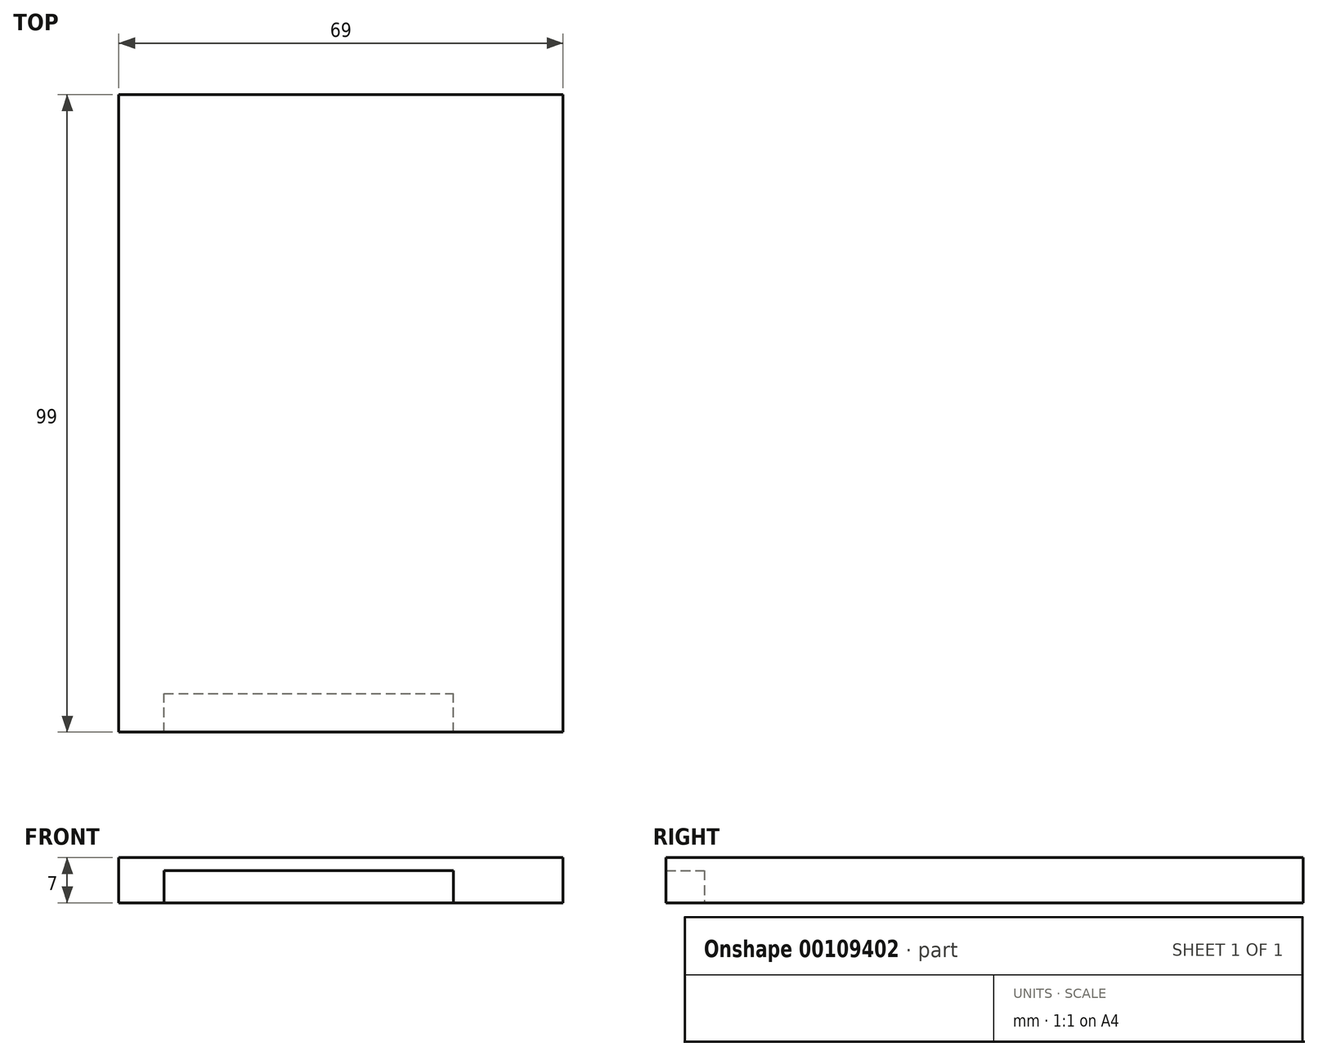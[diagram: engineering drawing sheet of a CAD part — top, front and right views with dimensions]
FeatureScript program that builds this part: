
annotation { "Feature Type Name" : "Feature", "Feature Type Description" : "" }
export const myFeature = defineFeature(function(context is Context, id is Id, definition is map)
    precondition{}
    {
        {
            var Q0;
            Q0=qCreatedBy(makeId("Top.planeOp"),FACE);
            var sketch = newSketch(context, id + "F0", { "sketchPlane" : qUnion([Q0])});
            skLineSegment(sketch, "E0.bottom", {"start": v(34.5, -49.5) * mm, "end": v(-34.5, -49.5) * mm});
            skLineSegment(sketch, "E0.top", {"start": v(34.5, 49.5) * mm, "end": v(-34.5, 49.5) * mm});
            skLineSegment(sketch, "E0.left", {"start": v(34.5, -49.5) * mm, "end": v(34.5, 49.5) * mm});
            skLineSegment(sketch, "E0.right", {"start": v(-34.5, -49.5) * mm, "end": v(-34.5, 49.5) * mm});
            skPoint(sketch, "E0.middle", {"position": v(0, 0) * mm});
            skSolve(sketch);
        }
        {
            var Q0;
            Q0 = qSketchRegion(id + "F0", true);
            extrude(context, id + "F2", {"entities" : qUnion([Q0]), "endBound" : BoundingType.SYMMETRIC, "depth" : 7 * mm});
        }
        {
            var Q0;
            Q0=makeQuery(id+"F2.opExtrude","CAP_FACE",FACE,{"disambiguationData":[OSD([sQuery(id+"F0.wireOp",EDGE,"E0.bottom"),sQuery(id+"F0.wireOp",EDGE,"E0.top"),sQuery(id+"F0.wireOp",EDGE,"E0.left"),sQuery(id+"F0.wireOp",EDGE,"E0.right")])],"isStart":true});
            var sketch = newSketch(context, id + "F1", { "sketchPlane" : qUnion([Q0])});
            skLineSegment(sketch, "E1.bottom", {"start": v(-27.5, 49.5) * mm, "end": v(17.5, 49.5) * mm});
            skLineSegment(sketch, "E1.top", {"start": v(-27.5, 43.5) * mm, "end": v(17.5, 43.5) * mm});
            skLineSegment(sketch, "E1.left", {"start": v(-27.5, 49.5) * mm, "end": v(-27.5, 43.5) * mm});
            skLineSegment(sketch, "E1.right", {"start": v(17.5, 49.5) * mm, "end": v(17.5, 43.5) * mm});
            skSolve(sketch);
        }
        {
            var Q0;
            Q0 = qSketchRegion(id + "F1", true);
            extrude(context, id + "F3", {"entities" : qUnion([Q0]), "operationType" : NewBodyOperationType.REMOVE, "oppositeDirection" : true, "depth" : 5 * mm});
        }
    });
